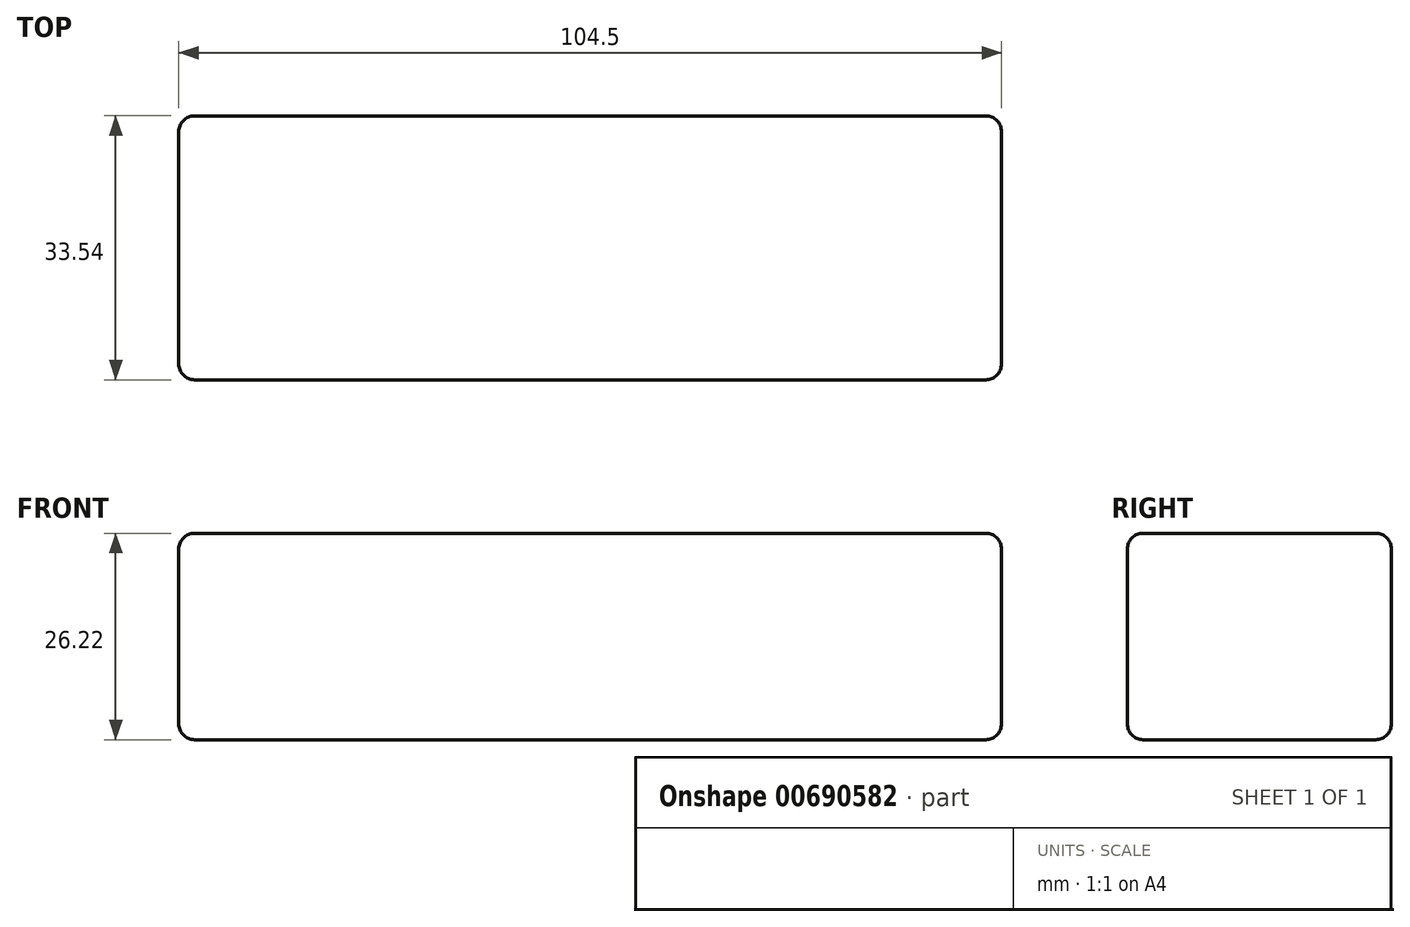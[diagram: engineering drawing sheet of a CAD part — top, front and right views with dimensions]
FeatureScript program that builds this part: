
annotation { "Feature Type Name" : "Feature", "Feature Type Description" : "" }
export const myFeature = defineFeature(function(context is Context, id is Id, definition is map)
    precondition{}
    {
        {
            var Q0;
            Q0=qCreatedBy(makeId("Top.planeOp"),FACE);
            var sketch = newSketch(context, id + "F0", { "sketchPlane" : qUnion([Q0])});
            skLineSegment(sketch, "E0.bottom", {"start": v(-52.25, 16.76) * mm, "end": v(52.25, 16.76) * mm});
            skLineSegment(sketch, "E0.top", {"start": v(-52.25, -16.77) * mm, "end": v(52.25, -16.77) * mm});
            skLineSegment(sketch, "E0.left", {"start": v(-52.25, 16.76) * mm, "end": v(-52.25, -16.77) * mm});
            skLineSegment(sketch, "E0.right", {"start": v(52.25, 16.76) * mm, "end": v(52.25, -16.77) * mm});
            skPoint(sketch, "E0.middle", {"position": v(0, 0) * mm});
            skSolve(sketch);
        }
        {
            var Q0;
            Q0 = qSketchRegion(id + "F0", true);
            extrude(context, id + "F1", {"entities" : qUnion([Q0]), "depth" : 26.22 * mm, "offsetDistance" : 25 * mm, "symmetric" : true});
        }
        {
            var Q0;
            Q0=makeQuery(id+"F1.opExtrude","SWEPT_FACE",FACE,{"disambiguationData":[OSD([sQuery(id+"F0.wireOp",EDGE,"E0.top")])]});
            var Q1;
            Q1=makeQuery(id+"F1.opExtrude","CAP_FACE",FACE,{"disambiguationData":[OSD([sQuery(id+"F0.wireOp",EDGE,"E0.bottom"),sQuery(id+"F0.wireOp",EDGE,"E0.top"),sQuery(id+"F0.wireOp",EDGE,"E0.left"),sQuery(id+"F0.wireOp",EDGE,"E0.right")])],"isStart":false});
            var Q2;
            Q2=makeQuery(id+"F1.opExtrude","SWEPT_FACE",FACE,{"disambiguationData":[OSD([sQuery(id+"F0.wireOp",EDGE,"E0.bottom")])]});
            var Q3;
            Q3=makeQuery(id+"F1.opExtrude","SWEPT_FACE",FACE,{"disambiguationData":[OSD([sQuery(id+"F0.wireOp",EDGE,"E0.right")])]});
            var Q4;
            Q4=makeQuery(id+"F1.opExtrude","CAP_FACE",FACE,{"disambiguationData":[OSD([sQuery(id+"F0.wireOp",EDGE,"E0.bottom"),sQuery(id+"F0.wireOp",EDGE,"E0.top"),sQuery(id+"F0.wireOp",EDGE,"E0.left"),sQuery(id+"F0.wireOp",EDGE,"E0.right")])],"isStart":true});
            fillet(context, id + "F2", {"entities" : qUnion([Q0, Q1, Q2, Q3, Q4]), "radius" : 2 * mm, "tangentPropagation" : true, "allowEdgeOverflow" : false});
        }
    });
